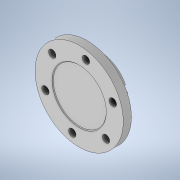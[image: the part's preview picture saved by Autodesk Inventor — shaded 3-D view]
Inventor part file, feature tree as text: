
AUTODESK INVENTOR PART (.ipt)
format: ipt  version: 2020 (Build 240168000, 168)  size: 172,544 bytes
history: native  units: mm
features: extrude x4, sketch x4, reference x4, other x4, plane x2, fillet x1
ambient origin geometry x8: Origin, YZ Plane, XZ Plane, XY Plane, X Axis, Y Axis, Z Axis, Center Point
bodies: 实体1 (feature_tree)
feature tree (19):
  plane  "工作平面1"
  extrude  "拉伸1"  Depth=12.0mm
  extrude  "拉伸2"  Depth=20.0mm TaperAngle=0.0deg
  extrude  "拉伸3"  Depth=1.0mm TaperAngle=0.0deg
  fillet  "圆角1"  Radius=1.0mm
  extrude  "拉伸4"  Depth=8.0mm TaperAngle=0.0deg
  plane  "工作平面2"
  sketch  "草图1"  dims[d0=12.0mm d1=0.0mm d2=80.0mm]
  reference  "参考1"
  reference  "参考2"
  reference  "参考3"
  sketch  "草图2"  dims[d3=70.0mm d4=20.0mm d5=0.0mm]
  reference  "参考4"
  sketch  "草图3"  dims[d6=80.0mm d7=1.0mm d8=0.0mm d9=1.0mm]
  sketch  "草图4"  dims[d10=8.0mm d11=8.0mm d12=0.0mm]
  other  "<userpath>\Desktop\ME_course_project\课设试试\shaft_try_1.iam"
  other  "shaft_try_1.iam"
  other  "xia(1):1"
  other  "轴承端盖1:1"
